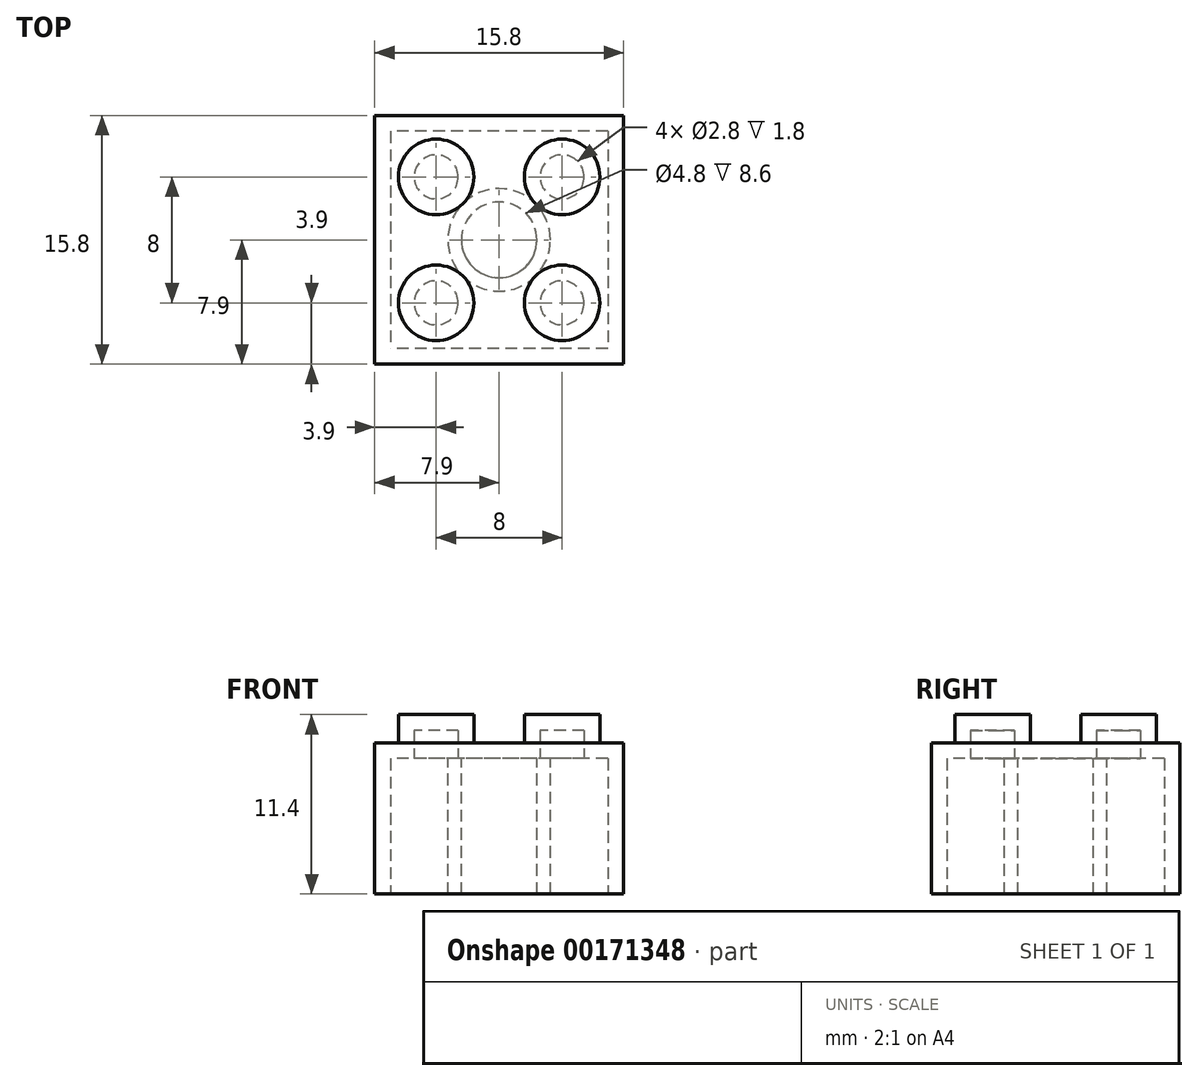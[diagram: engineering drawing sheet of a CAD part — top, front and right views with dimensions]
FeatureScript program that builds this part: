
annotation { "Feature Type Name" : "Feature", "Feature Type Description" : "" }
export const myFeature = defineFeature(function(context is Context, id is Id, definition is map)
    precondition{}
    {
        {
            var Q0;
            Q0=qCreatedBy(makeId("Top.planeOp"),FACE);
            var sketch = newSketch(context, id + "F0", { "sketchPlane" : qUnion([Q0])});
            skLineSegment(sketch, "E0.bottom", {"start": v(7.9, 7.9) * mm, "end": v(-7.9, 7.9) * mm});
            skLineSegment(sketch, "E0.top", {"start": v(7.9, -7.9) * mm, "end": v(-7.9, -7.9) * mm});
            skLineSegment(sketch, "E0.left", {"start": v(7.9, 7.9) * mm, "end": v(7.9, -7.9) * mm});
            skLineSegment(sketch, "E0.right", {"start": v(-7.9, 7.9) * mm, "end": v(-7.9, -7.9) * mm});
            skPoint(sketch, "E0.middle", {"position": v(0, 0) * mm});
            skSolve(sketch);
        }
        {
            var Q0;
            Q0 = qSketchRegion(id + "F0", true);
            extrude(context, id + "F1", {"entities" : qUnion([Q0]), "depth" : 9.6 * mm});
        }
        {
            var Q0;
            Q0=makeQuery(id+"F1.opExtrude","CAP_FACE",FACE,{"disambiguationData":[OSD([sQuery(id+"F0.wireOp",EDGE,"E0.bottom"),sQuery(id+"F0.wireOp",EDGE,"E0.top"),sQuery(id+"F0.wireOp",EDGE,"E0.left"),sQuery(id+"F0.wireOp",EDGE,"E0.right")])],"isStart":false});
            var sketch = newSketch(context, id + "F2", { "sketchPlane" : qUnion([Q0])});
            skLineSegment(sketch, "E1.bottom", {"start": v(4, 4) * mm, "end": v(-4, 4) * mm, "construction": true});
            skLineSegment(sketch, "E1.top", {"start": v(4, -4) * mm, "end": v(-4, -4) * mm, "construction": true});
            skLineSegment(sketch, "E1.left", {"start": v(4, 4) * mm, "end": v(4, -4) * mm, "construction": true});
            skLineSegment(sketch, "E1.right", {"start": v(-4, 4) * mm, "end": v(-4, -4) * mm, "construction": true});
            skPoint(sketch, "E1.middle", {"position": v(0, 0) * mm});
            skCircle(sketch, "E2", {"center": v(-4, 4) * mm, "radius": 2.4 * mm});
            skCircle(sketch, "E3", {"center": v(4, 4) * mm, "radius": 2.4 * mm});
            skCircle(sketch, "E4", {"center": v(4, -4) * mm, "radius": 2.4 * mm});
            skCircle(sketch, "E5", {"center": v(-4, -4) * mm, "radius": 2.4 * mm});
            skPoint(sketch, "E6", {"position": v(-6.4, 4) * mm});
            skLineSegment(sketch, "E7", {"start": v(-4, 4) * mm, "end": v(-4, 7.9) * mm, "construction": true});
            skLineSegment(sketch, "E8", {"start": v(-4, 4) * mm, "end": v(-7.9, 4) * mm, "construction": true});
            skSolve(sketch);
        }
        {
            var Q0;
            Q0 = qSketchRegion(id + "F2", true);
            extrude(context, id + "F3", {"entities" : qUnion([Q0]), "operationType" : NewBodyOperationType.ADD, "depth" : 1.8 * mm});
        }
        {
            var Q0;
            Q0=makeQuery(id+"F1.opExtrude","CAP_FACE",FACE,{"disambiguationData":[OSD([sQuery(id+"F0.wireOp",EDGE,"E0.bottom"),sQuery(id+"F0.wireOp",EDGE,"E0.top"),sQuery(id+"F0.wireOp",EDGE,"E0.left"),sQuery(id+"F0.wireOp",EDGE,"E0.right")])],"isStart":true});
            shell(context, id + "F4", {"entities" : qUnion([Q0]), "thickness" : 1 * mm});
        }
        {
            var Q0;
            Q0=makeQuery(id+"F4.opShell","OFFSET_FACE",FACE,{"disambiguationData":[OSD([sQuery(id+"F0.wireOp",EDGE,"E0.bottom"),sQuery(id+"F0.wireOp",EDGE,"E0.top"),sQuery(id+"F0.wireOp",EDGE,"E0.left"),sQuery(id+"F0.wireOp",EDGE,"E0.right")])]});
            var sketch = newSketch(context, id + "F5", { "sketchPlane" : qUnion([Q0])});
            skCircle(sketch, "E9", {"center": v(0, 0) * mm, "radius": 3.25 * mm});
            skCircle(sketch, "E10", {"center": v(0, 0) * mm, "radius": 2.4 * mm});
            skSolve(sketch);
        }
        {
            var Q0;
            Q0 = qSketchRegion(id + "F5", true);
            var Q1;
            Q1=makeQuery(id+"F1.opExtrude","CAP_FACE",FACE,{"disambiguationData":[OSD([sQuery(id+"F0.wireOp",EDGE,"E0.bottom"),sQuery(id+"F0.wireOp",EDGE,"E0.top"),sQuery(id+"F0.wireOp",EDGE,"E0.left"),sQuery(id+"F0.wireOp",EDGE,"E0.right")])],"isStart":true});
            extrude(context, id + "F6", {"entities" : qUnion([Q0]), "operationType" : NewBodyOperationType.ADD, "endBound" : BoundingType.UP_TO_SURFACE, "endBoundEntityFace" : qUnion([Q1]), "depth" : 25 * mm});
        }
    });
